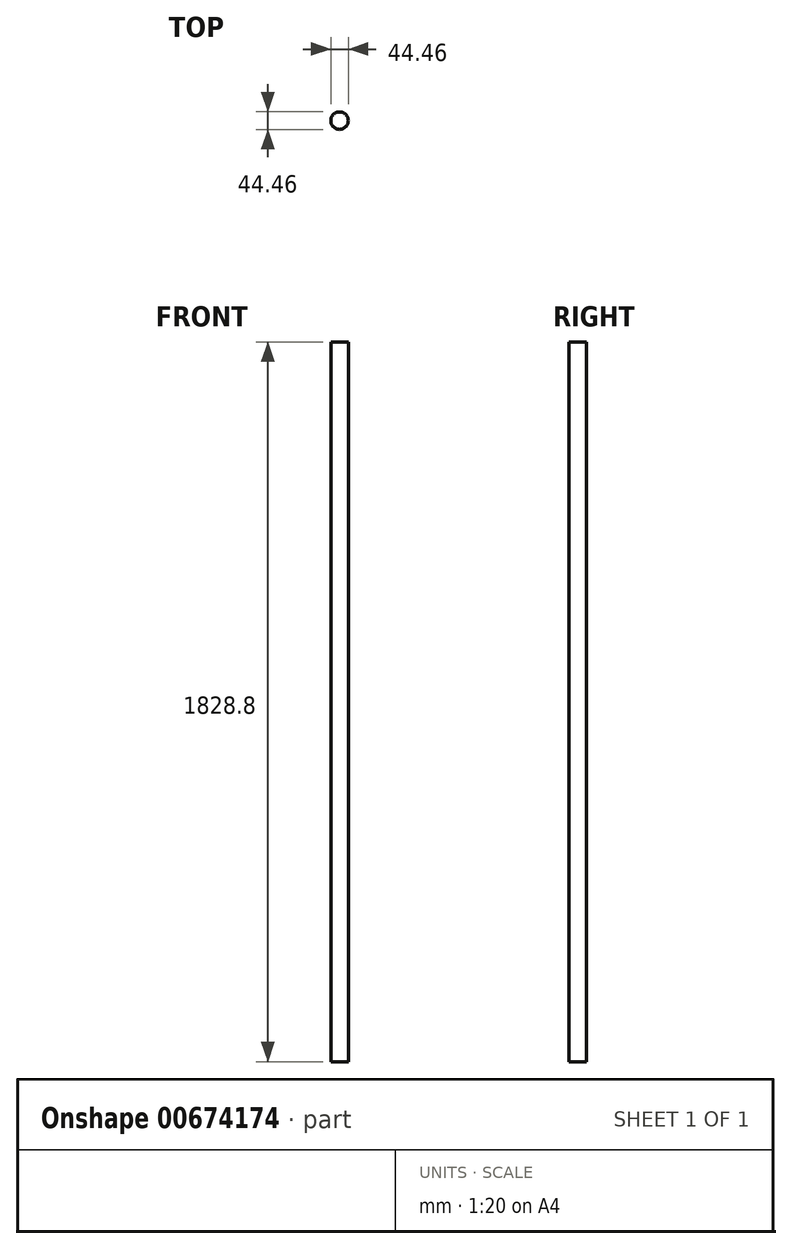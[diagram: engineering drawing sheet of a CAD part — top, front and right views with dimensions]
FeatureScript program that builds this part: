
annotation { "Feature Type Name" : "Feature", "Feature Type Description" : "" }
export const myFeature = defineFeature(function(context is Context, id is Id, definition is map)
    precondition{}
    {
        {
            var Q0;
            Q0=qCreatedBy(makeId("Top.planeOp"),FACE);
            var sketch = newSketch(context, id + "F0", { "sketchPlane" : qUnion([Q0])});
            skCircle(sketch, "E0", {"center": v(0, 0) * mm, "radius": 22.23 * mm});
            skSolve(sketch);
        }
        {
            var Q0;
            Q0=makeQuery(id+"F0.imprint","IMPRINT",FACE,{"disambiguationData":[TD([[makeQuery(id+"F0.imprint","IMPRINT",EDGE,{"derivedFrom":sQuery(id+"F0.wireOp",EDGE,"E0")}),1.0]])]});
            extrude(context, id + "F1", {"entities" : qUnion([Q0]), "depth" : 1828.8 * mm, "offsetDistance" : 25.4 * mm});
        }
    });
